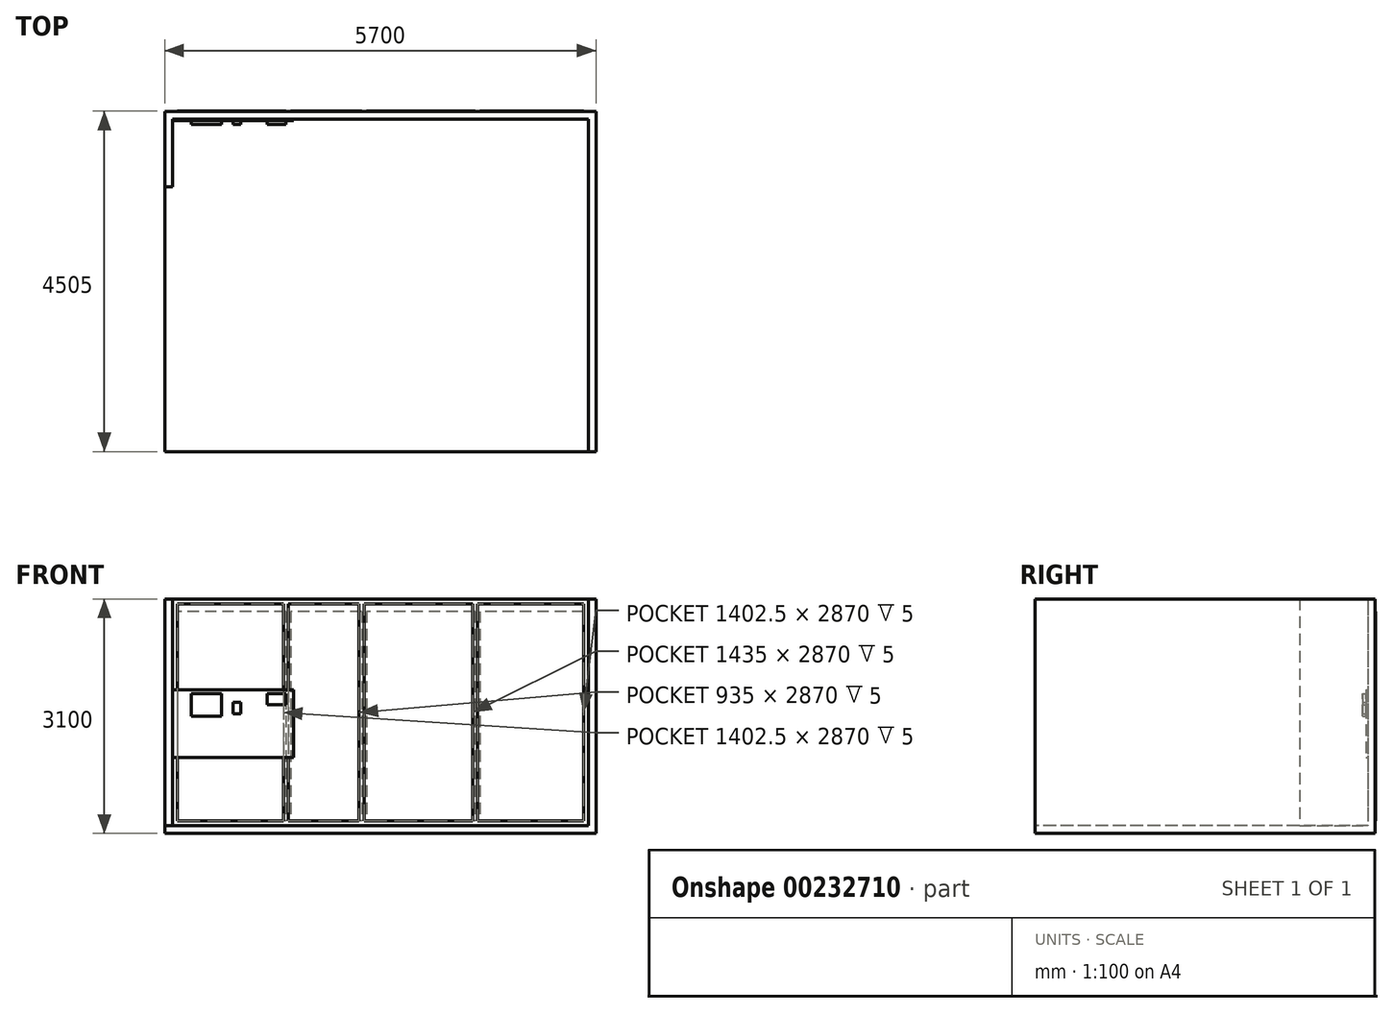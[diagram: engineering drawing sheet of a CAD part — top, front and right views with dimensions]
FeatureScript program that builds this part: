
annotation { "Feature Type Name" : "Feature", "Feature Type Description" : "" }
export const myFeature = defineFeature(function(context is Context, id is Id, definition is map)
    precondition{}
    {
        {
            var Q0;
            Q0=qCreatedBy(makeId("Top.planeOp"),FACE);
            var sketch = newSketch(context, id + "F0", { "sketchPlane" : qUnion([Q0])});
            skLineSegment(sketch, "E0.bottom", {"start": v(0, 0) * mm, "end": v(5700, 0) * mm});
            skLineSegment(sketch, "E0.top", {"start": v(0, -4500) * mm, "end": v(5700, -4500) * mm});
            skLineSegment(sketch, "E0.left", {"start": v(0, 0) * mm, "end": v(0, -4500) * mm});
            skLineSegment(sketch, "E0.right", {"start": v(5700, 0) * mm, "end": v(5700, -4500) * mm});
            skSolve(sketch);
        }
        {
            var Q0;
            Q0 = qSketchRegion(id + "F0", true);
            extrude(context, id + "F1", {"entities" : qUnion([Q0]), "depth" : 100 * mm});
        }
        {
            var Q0;
            Q0=makeQuery(id+"F1.opExtrude","CAP_FACE",FACE,{"disambiguationData":[OSD([sQuery(id+"F0.wireOp",EDGE,"E0.bottom"),sQuery(id+"F0.wireOp",EDGE,"E0.top"),sQuery(id+"F0.wireOp",EDGE,"E0.left"),sQuery(id+"F0.wireOp",EDGE,"E0.right")])],"isStart":false});
            var sketch = newSketch(context, id + "F2", { "sketchPlane" : qUnion([Q0])});
            skLineSegment(sketch, "E1", {"start": v(0, 0) * mm, "end": v(0, -1000) * mm});
            skLineSegment(sketch, "E2", {"start": v(0, -1000) * mm, "end": v(100, -1000) * mm});
            skLineSegment(sketch, "E3", {"start": v(100, -1000) * mm, "end": v(100, -100) * mm});
            skLineSegment(sketch, "E4", {"start": v(100, -100) * mm, "end": v(5600, -100) * mm});
            skLineSegment(sketch, "E5", {"start": v(5600, -100) * mm, "end": v(5600, -4500) * mm});
            skLineSegment(sketch, "E6", {"start": v(5600, -4500) * mm, "end": v(5700, -4500) * mm});
            skLineSegment(sketch, "E7", {"start": v(5700, -4500) * mm, "end": v(5700, 0) * mm});
            skLineSegment(sketch, "E8", {"start": v(5700, 0) * mm, "end": v(0, 0) * mm});
            skSolve(sketch);
        }
        {
            var Q0;
            Q0 = qSketchRegion(id + "F2", true);
            extrude(context, id + "F3", {"entities" : qUnion([Q0]), "operationType" : NewBodyOperationType.ADD, "depth" : 3000 * mm});
        }
        {
            var Q0;
            Q0=makeQuery(id+"F3.opExtrude","SWEPT_FACE",FACE,{"disambiguationData":[OSD([sQuery(id+"F2.wireOp",EDGE,"E4")])]});
            var sketch = newSketch(context, id + "F4", { "sketchPlane" : qUnion([Q0])});
            skLineSegment(sketch, "E9", {"start": v(1600, 3100) * mm, "end": v(1600, 100) * mm, "construction": true});
            skLineSegment(sketch, "E10", {"start": v(2600, 3100) * mm, "end": v(2600, 100) * mm, "construction": true});
            skLineSegment(sketch, "E11", {"start": v(4100, 3100) * mm, "end": v(4100, 100) * mm, "construction": true});
            skLineSegment(sketch, "E12.bottom", {"start": v(165, 3035) * mm, "end": v(1567.5, 3035) * mm});
            skLineSegment(sketch, "E12.top", {"start": v(165, 165) * mm, "end": v(1567.5, 165) * mm});
            skLineSegment(sketch, "E12.left", {"start": v(165, 3035) * mm, "end": v(165, 165) * mm});
            skLineSegment(sketch, "E12.right", {"start": v(1567.5, 3035) * mm, "end": v(1567.5, 165) * mm});
            skLineSegment(sketch, "E13.bottom", {"start": v(1632.5, 3035) * mm, "end": v(2567.5, 3035) * mm});
            skLineSegment(sketch, "E13.top", {"start": v(1632.5, 165) * mm, "end": v(2567.5, 165) * mm});
            skLineSegment(sketch, "E13.left", {"start": v(1632.5, 3035) * mm, "end": v(1632.5, 165) * mm});
            skLineSegment(sketch, "E13.right", {"start": v(2567.5, 3035) * mm, "end": v(2567.5, 165) * mm});
            skLineSegment(sketch, "E14.bottom", {"start": v(2632.5, 3035) * mm, "end": v(4067.5, 3035) * mm});
            skLineSegment(sketch, "E14.top", {"start": v(2632.5, 165) * mm, "end": v(4067.5, 165) * mm});
            skLineSegment(sketch, "E14.left", {"start": v(2632.5, 3035) * mm, "end": v(2632.5, 165) * mm});
            skLineSegment(sketch, "E14.right", {"start": v(4067.5, 3035) * mm, "end": v(4067.5, 165) * mm});
            skLineSegment(sketch, "E15.bottom", {"start": v(4132.5, 3035) * mm, "end": v(5535, 3035) * mm});
            skLineSegment(sketch, "E15.top", {"start": v(4132.5, 165) * mm, "end": v(5535, 165) * mm});
            skLineSegment(sketch, "E15.left", {"start": v(4132.5, 3035) * mm, "end": v(4132.5, 165) * mm});
            skLineSegment(sketch, "E15.right", {"start": v(5535, 3035) * mm, "end": v(5535, 165) * mm});
            skSolve(sketch);
        }
        {
            var Q0;
            Q0=makeQuery(id+"F4.imprint","IMPRINT",FACE,{"disambiguationData":[TD([[makeQuery(id+"F4.imprint","IMPRINT",EDGE,{"derivedFrom":sQuery(id+"F4.wireOp",EDGE,"E12.bottom")}),-1.0]])]});
            var Q1;
            Q1=makeQuery(id+"F4.imprint","IMPRINT",FACE,{"disambiguationData":[TD([[makeQuery(id+"F4.imprint","IMPRINT",EDGE,{"derivedFrom":sQuery(id+"F4.wireOp",EDGE,"E13.bottom")}),-1.0]])]});
            var Q2;
            Q2=makeQuery(id+"F4.imprint","IMPRINT",FACE,{"disambiguationData":[TD([[makeQuery(id+"F4.imprint","IMPRINT",EDGE,{"derivedFrom":sQuery(id+"F4.wireOp",EDGE,"E14.bottom")}),-1.0]])]});
            var Q3;
            Q3=makeQuery(id+"F4.imprint","IMPRINT",FACE,{"disambiguationData":[TD([[makeQuery(id+"F4.imprint","IMPRINT",EDGE,{"derivedFrom":sQuery(id+"F4.wireOp",EDGE,"E15.bottom")}),-1.0]])]});
            extrude(context, id + "F5", {"entities" : qUnion([Q0, Q1, Q2, Q3]), "operationType" : NewBodyOperationType.REMOVE, "oppositeDirection" : true, "depth" : 5 * mm});
        }
        {
            var Q0;
            Q0=makeQuery(id+"F3.opExtrude","SWEPT_FACE",FACE,{"disambiguationData":[OSD([sQuery(id+"F2.wireOp",EDGE,"E4")])]});
            var sketch = newSketch(context, id + "F6", { "sketchPlane" : qUnion([Q0])});
            skLineSegment(sketch, "E16.bottom", {"start": v(100, 1900) * mm, "end": v(1700, 1900) * mm});
            skLineSegment(sketch, "E16.top", {"start": v(100, 1000) * mm, "end": v(1700, 1000) * mm});
            skLineSegment(sketch, "E16.left", {"start": v(100, 1900) * mm, "end": v(100, 1000) * mm});
            skLineSegment(sketch, "E16.right", {"start": v(1700, 1900) * mm, "end": v(1700, 1000) * mm});
            skSolve(sketch);
        }
        {
            var Q0;
            Q0 = qSketchRegion(id + "F6", true);
            extrude(context, id + "F7", {"entities" : qUnion([Q0]), "operationType" : NewBodyOperationType.ADD, "depth" : 20 * mm});
        }
        {
            var Q0;
            Q0=makeQuery(id+"F7.opExtrude","CAP_FACE",FACE,{"disambiguationData":[OSD([sQuery(id+"F6.wireOp",EDGE,"E16.bottom"),sQuery(id+"F6.wireOp",EDGE,"E16.top"),sQuery(id+"F6.wireOp",EDGE,"E16.left"),sQuery(id+"F6.wireOp",EDGE,"E16.right")])],"isStart":false});
            var sketch = newSketch(context, id + "F8", { "sketchPlane" : qUnion([Q0])});
            skLineSegment(sketch, "E17.top", {"start": v(350, 1550) * mm, "end": v(750, 1550) * mm});
            skLineSegment(sketch, "E17.right", {"start": v(750, 1850) * mm, "end": v(750, 1550) * mm});
            skLineSegment(sketch, "E18.bottom", {"start": v(900, 1730) * mm, "end": v(1000, 1730) * mm});
            skLineSegment(sketch, "E18.top", {"start": v(900, 1580) * mm, "end": v(1000, 1580) * mm});
            skLineSegment(sketch, "E18.left", {"start": v(900, 1730) * mm, "end": v(900, 1580) * mm});
            skLineSegment(sketch, "E18.right", {"start": v(1000, 1730) * mm, "end": v(1000, 1580) * mm});
            skLineSegment(sketch, "E19", {"start": v(350, 1550) * mm, "end": v(350, 1850) * mm});
            skLineSegment(sketch, "E20", {"start": v(350, 1850) * mm, "end": v(750, 1850) * mm});
            skLineSegment(sketch, "E21.bottom", {"start": v(1350, 1850) * mm, "end": v(1600, 1850) * mm});
            skLineSegment(sketch, "E21.top", {"start": v(1350, 1700) * mm, "end": v(1600, 1700) * mm});
            skLineSegment(sketch, "E21.left", {"start": v(1350, 1850) * mm, "end": v(1350, 1700) * mm});
            skLineSegment(sketch, "E21.right", {"start": v(1600, 1850) * mm, "end": v(1600, 1700) * mm});
            skSolve(sketch);
        }
        {
            var Q0;
            Q0 = qSketchRegion(id + "F8", true);
            extrude(context, id + "F9", {"entities" : qUnion([Q0]), "operationType" : NewBodyOperationType.ADD, "depth" : 50 * mm});
        }
        {
            var Q0;
            Q0=makeQuery(id+"F3.boolean.opBoolean","MERGE",FACE,{"derivedFrom":[makeQuery(id+"F1.opExtrude","SWEPT_FACE",FACE,{"disambiguationData":[OSD([sQuery(id+"F0.wireOp",EDGE,"E0.bottom")])]}),makeQuery(id+"F3.opExtrude","SWEPT_FACE",FACE,{"disambiguationData":[OSD([sQuery(id+"F2.wireOp",EDGE,"E8")])]})]});
            var sketch = newSketch(context, id + "F10", { "sketchPlane" : qUnion([Q0])});
            skLineSegment(sketch, "E22", {"start": v(-4132.5, 3100) * mm, "end": v(-4132.5, 0) * mm, "construction": true});
            skLineSegment(sketch, "E23", {"start": v(-2632.5, 3100) * mm, "end": v(-2632.5, 0) * mm, "construction": true});
            skLineSegment(sketch, "E24", {"start": v(-1632.5, 3100) * mm, "end": v(-1632.5, 0) * mm, "construction": true});
            skLineSegment(sketch, "E25.bottom", {"start": v(-5535, 2935) * mm, "end": v(-4165, 2935) * mm});
            skLineSegment(sketch, "E25.top", {"start": v(-5535, 165) * mm, "end": v(-4165, 165) * mm});
            skLineSegment(sketch, "E25.left", {"start": v(-5535, 2935) * mm, "end": v(-5535, 165) * mm});
            skLineSegment(sketch, "E25.right", {"start": v(-4165, 2935) * mm, "end": v(-4165, 165) * mm});
            skLineSegment(sketch, "E26.bottom", {"start": v(-4100, 2935) * mm, "end": v(-2665, 2935) * mm});
            skLineSegment(sketch, "E26.top", {"start": v(-4100, 165) * mm, "end": v(-2665, 165) * mm});
            skLineSegment(sketch, "E26.left", {"start": v(-4100, 2935) * mm, "end": v(-4100, 165) * mm});
            skLineSegment(sketch, "E26.right", {"start": v(-2665, 2935) * mm, "end": v(-2665, 165) * mm});
            skLineSegment(sketch, "E27.bottom", {"start": v(-2600, 2935) * mm, "end": v(-1665, 2935) * mm});
            skLineSegment(sketch, "E27.top", {"start": v(-2600, 165) * mm, "end": v(-1665, 165) * mm});
            skLineSegment(sketch, "E27.left", {"start": v(-2600, 2935) * mm, "end": v(-2600, 165) * mm});
            skLineSegment(sketch, "E27.right", {"start": v(-1665, 2935) * mm, "end": v(-1665, 165) * mm});
            skLineSegment(sketch, "E28.bottom", {"start": v(-1600, 2935) * mm, "end": v(-165, 2935) * mm});
            skLineSegment(sketch, "E28.top", {"start": v(-1600, 165) * mm, "end": v(-165, 165) * mm});
            skLineSegment(sketch, "E28.left", {"start": v(-1600, 2935) * mm, "end": v(-1600, 165) * mm});
            skLineSegment(sketch, "E28.right", {"start": v(-165, 2935) * mm, "end": v(-165, 165) * mm});
            skSolve(sketch);
        }
        {
            var Q0;
            Q0 = qSketchRegion(id + "F10", true);
            extrude(context, id + "F11", {"entities" : qUnion([Q0]), "operationType" : NewBodyOperationType.ADD, "depth" : 5 * mm});
        }
    });
